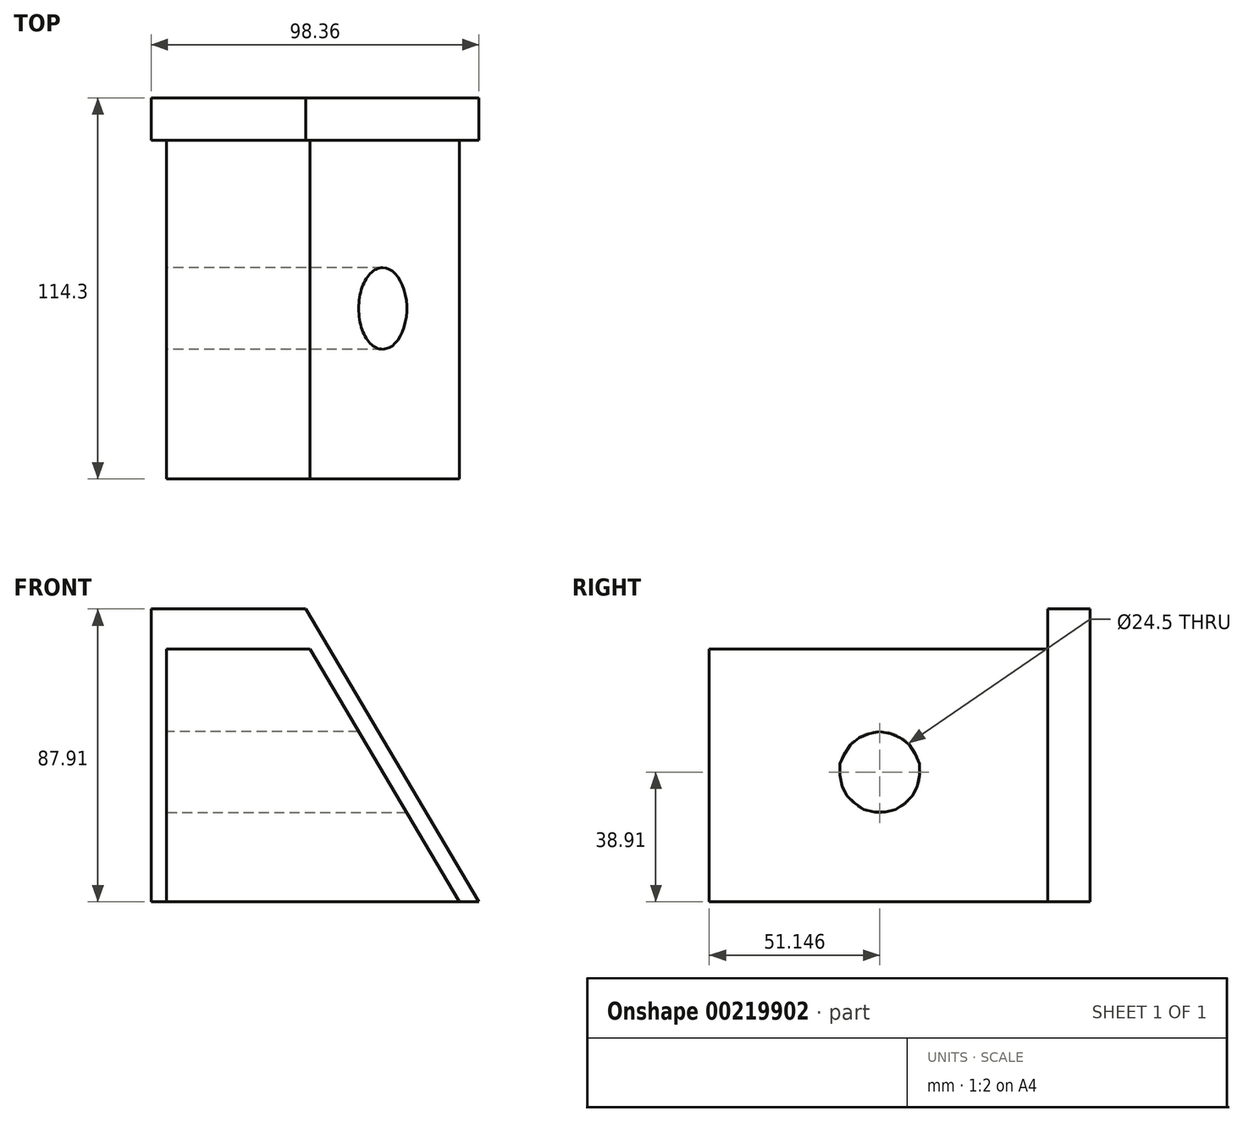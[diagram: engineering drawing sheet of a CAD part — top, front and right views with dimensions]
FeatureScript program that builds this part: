
annotation { "Feature Type Name" : "Feature", "Feature Type Description" : "" }
export const myFeature = defineFeature(function(context is Context, id is Id, definition is map)
    precondition{}
    {
        {
            var Q0;
            Q0=qCreatedBy(makeId("Front.planeOp"),FACE);
            var sketch = newSketch(context, id + "F0", { "sketchPlane" : qUnion([Q0])});
            skLineSegment(sketch, "E0", {"start": v(-38.8, 49) * mm, "end": v(7.56, 49) * mm});
            skLineSegment(sketch, "E1", {"start": v(7.56, 49) * mm, "end": v(59.57, -38.9) * mm});
            skLineSegment(sketch, "E2", {"start": v(59.57, -38.9) * mm, "end": v(-38.8, -38.9) * mm});
            skLineSegment(sketch, "E3", {"start": v(-38.8, -38.9) * mm, "end": v(-38.8, 49) * mm});
            skSolve(sketch);
        }
        {
            var Q0;
            Q0 = qSketchRegion(id + "F0", true);
            extrude(context, id + "F1", {"entities" : qUnion([Q0]), "depth" : 12.7 * mm});
        }
        {
            var Q0;
            Q0=makeQuery(id+"F1.opExtrude","CAP_FACE",FACE,{"disambiguationData":[OSD([sQuery(id+"F0.wireOp",EDGE,"E0"),sQuery(id+"F0.wireOp",EDGE,"E1"),sQuery(id+"F0.wireOp",EDGE,"E2"),sQuery(id+"F0.wireOp",EDGE,"E3")])],"isStart":false});
            var sketch = newSketch(context, id + "F2", { "sketchPlane" : qUnion([Q0])});
            skLineSegment(sketch, "E4", {"start": v(-34.17, 36.95) * mm, "end": v(8.85, 36.95) * mm});
            skLineSegment(sketch, "E5", {"start": v(8.85, 36.95) * mm, "end": v(53.73, -38.9) * mm});
            skLineSegment(sketch, "E6", {"start": v(53.73, -38.9) * mm, "end": v(-34.17, -38.9) * mm});
            skLineSegment(sketch, "E7", {"start": v(-34.17, -38.9) * mm, "end": v(-34.17, 36.95) * mm});
            skSolve(sketch);
        }
        {
            var Q0;
            Q0 = qSketchRegion(id + "F2", true);
            extrude(context, id + "F3", {"entities" : qUnion([Q0]), "operationType" : NewBodyOperationType.ADD, "depth" : 101.6 * mm});
        }
        {
            var Q0;
            Q0=makeQuery(id+"F3.opExtrude","SWEPT_FACE",FACE,{"disambiguationData":[OSD([sQuery(id+"F2.wireOp",EDGE,"E7")])]});
            var sketch = newSketch(context, id + "F4", { "sketchPlane" : qUnion([Q0])});
            skCircle(sketch, "E8", {"center": v(63.15, 0) * mm, "radius": 12.25 * mm});
            skSolve(sketch);
        }
        {
            var Q0;
            Q0 = qSketchRegion(id + "F4", true);
            extrude(context, id + "F5", {"entities" : qUnion([Q0]), "operationType" : NewBodyOperationType.REMOVE, "oppositeDirection" : true, "depth" : 81.53 * mm});
        }
    });
